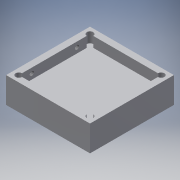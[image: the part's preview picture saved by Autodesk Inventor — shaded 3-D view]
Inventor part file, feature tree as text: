
AUTODESK INVENTOR PART (.ipt)
format: ipt  version: 2016 (Build 200138000, 138)  size: 161,792 bytes
history: native  units: mm
features: sketch x7, hole x4, extrude x3, projected_geometry x3
ambient origin geometry x8: Origin, YZ Plane, XZ Plane, XY Plane, X Axis, Y Axis, Z Axis, Center Point
bodies: Solid1 (feature_tree)
feature tree (17):
  extrude  "Extrusion1"  Depth=65.0mm
  hole  "Hole2"  [1 undecoded]
  extrude  "Extrusion3"  Depth=8.0mm TaperAngle=0.0deg
  hole  "Hole3"  [1 undecoded]
  extrude  "Extrusion4"  Depth=25.0mm
  hole  "Hole5"  [1 undecoded]
  hole  "Hole6"  [1 undecoded]
  sketch  "Sketch1"  dims[d0=65.0mm d1=65.0mm]
  sketch  "Sketch4"  dims[d2=20.0mm d3=0.0mm d15=55.1mm]
  sketch  "Sketch5"  dims[d16=55.1mm]
  sketch  "Sketch6"  dims[d17=5.0mm d18=6.0mm d19=4.0mm d20=2.0mm d21=90.0deg d22=8.0mm d23=0.0mm d24=8.0mm d25=0.0mm]
  projected_geometry  "Projected Loop1"
  sketch  "Sketch8"  dims[d26=15.0mm d27=15.0mm]
  projected_geometry  "Projected Loop2"
  sketch  "Sketch9"  dims[d28=3.242mm d29=6.0mm d30=4.0mm d31=2.0mm d32=90.0deg d33=8.0mm d34=20.594885mm d44=25.0mm]
  projected_geometry  "Projected Loop3"
  sketch  "Sketch10"  dims[d45=25.0mm d46=6.0mm d47=0.0mm d48=3.0mm d49=6.0mm d50=4.0mm d51=2.0mm d52=90.0deg d53=6.0mm d54=0.0mm d55=3.242mm d56=8.0mm d57=4.0mm d58=2.0mm d59=90.0deg d60=4.0mm d61=20.594885mm]
note: 4 required parameter values undecoded (feature->parameter linkage not recoverable at this tier; creation-order binding heuristic only, values carry confidence <= 0.55)
